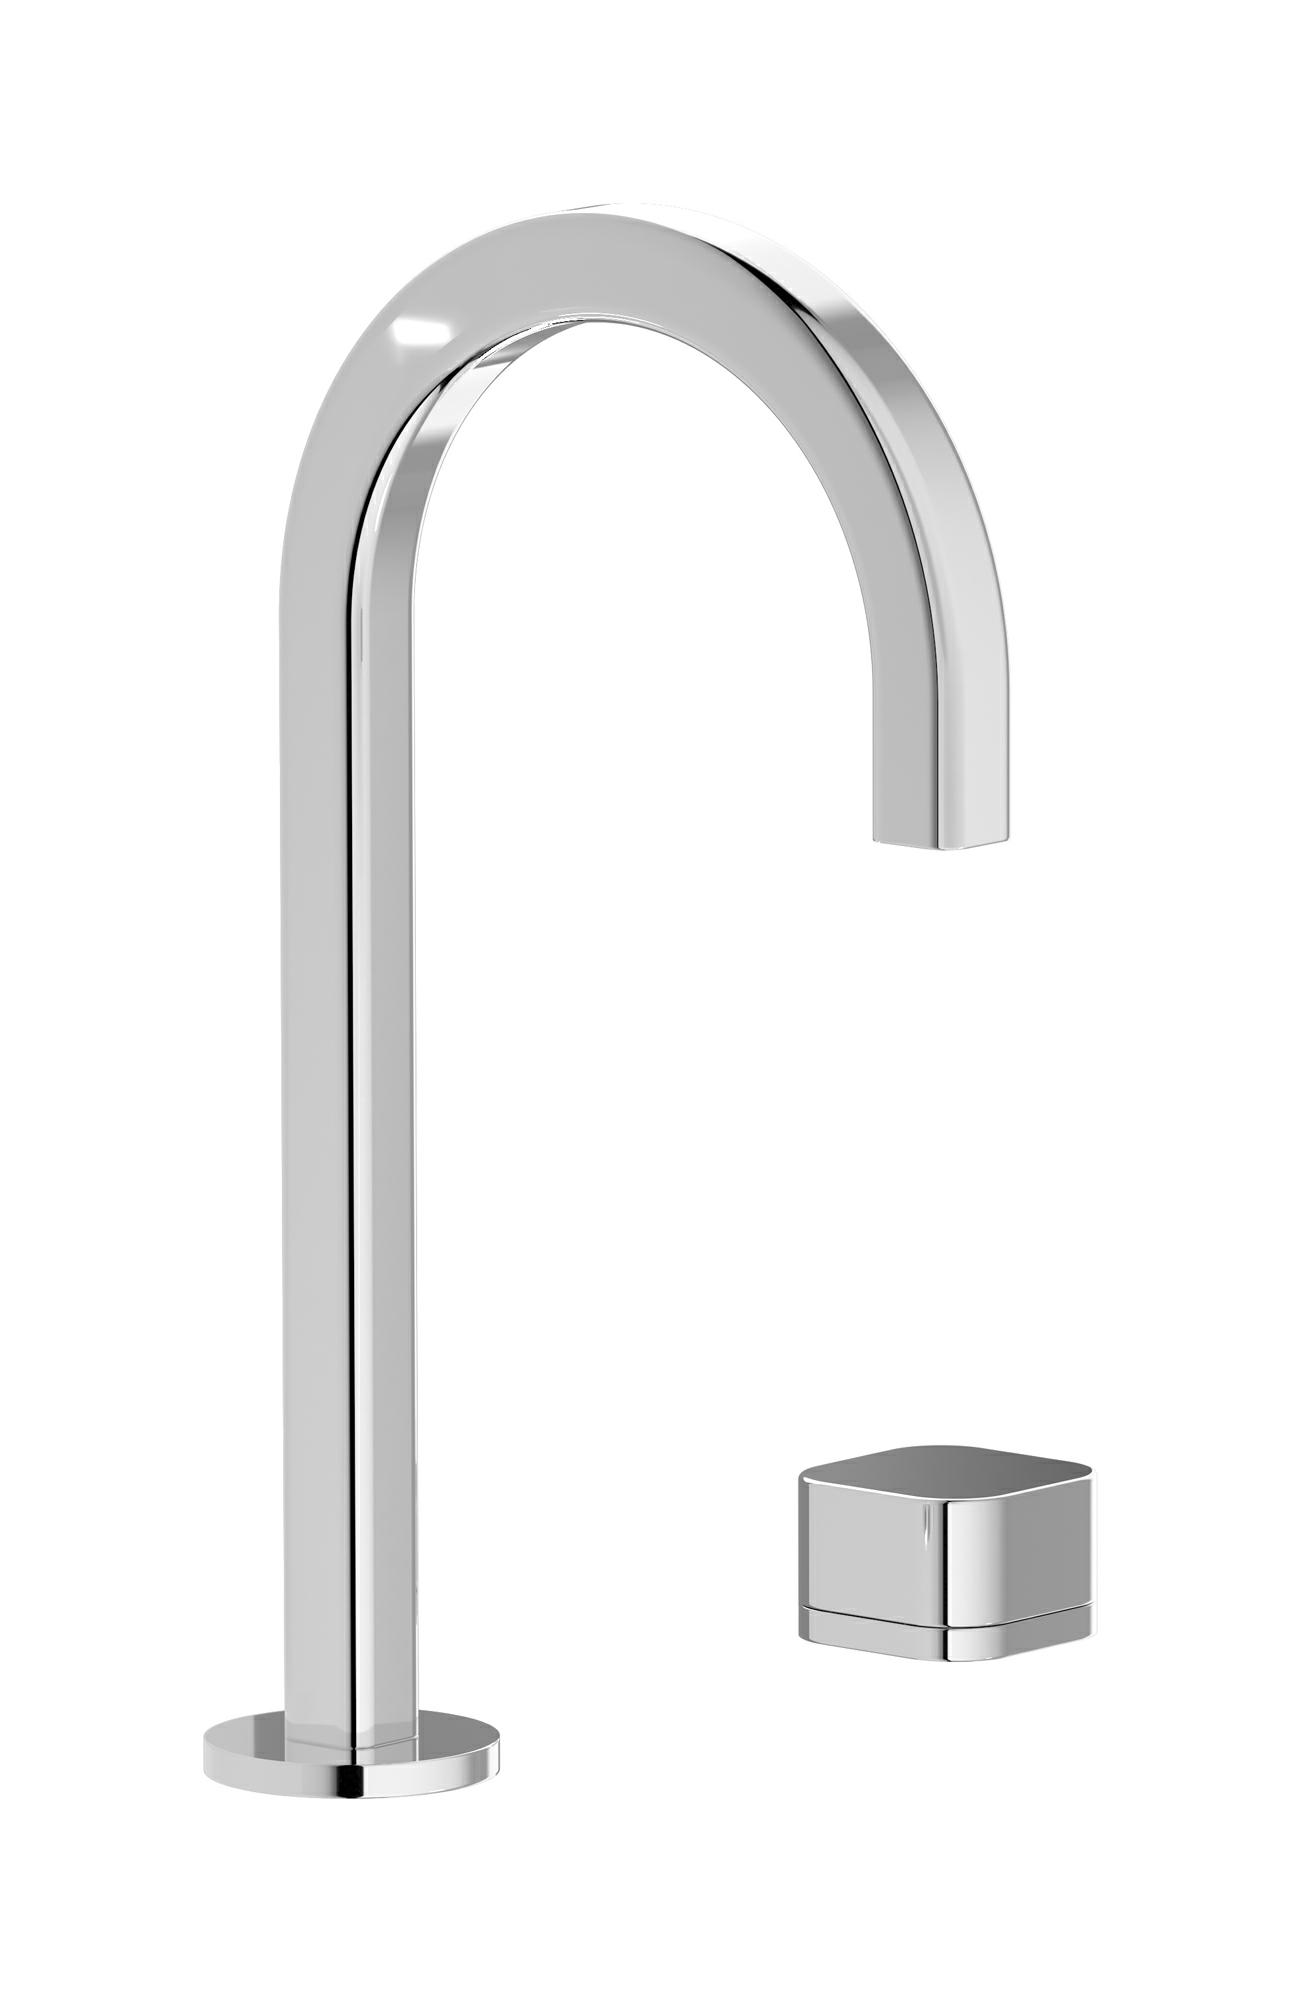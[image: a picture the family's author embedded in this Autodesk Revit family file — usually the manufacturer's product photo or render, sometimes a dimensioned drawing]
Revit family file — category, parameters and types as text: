
# Revit family: EO394_3
name_source: partatom
category: Apparecchi idraulici
units: mm (PartAtom-declared; Revit-internal decimal feet)

## family parameters
Basato su piano di lavoro = No
Condiviso = No
Mantieni orientamento annotazione = No
Numero OmniClass = 23.45.55.17
Punto di calcolo locali = No
Quota connettore circolare = Usa diametro
Sempre verticale = Sì
Taglio con vuoti quando caricato = No
Tipo di parte = Normale
Titolo OmniClass = Mixing Faucets

## types (12) — shared parameters
Cold water inlet = 10 mm  [stored 0.0328084 ft]
Commenti sul tipo = Washbasin
Connessione CW = No
Connessione HW = No
Connessione di scarico = No
Connessione di ventilazione = No
Descrizione = Washbasin two hole mixer
Hot water inlet = 10 mm  [stored 0.0328084 ft]
Produttore = IB Rubinetterie S.p.A.
URL = https://www.weareib.it
zero-valued in all types: Prospetto di default

## per-type parameters (varying)
| type | Finishes surface | Immagine tipo | Modello |
| Chrome | IB_Chrome | EO394CC_3.jpg | EO394CC_3 |
| Brushed nickel | IB_Brushed nickel | EO394SS_3.jpg | EO394SS_3 |
| Matt black | IB_matt black | EO394NP_3.jpg | EO394NP_3 |
| Natural brass | IB_Brass | EO394ON_3.jpg | EO394ON_3 |
| Black chrome | IB_Black chrome | EO394CF_3.jpg | EO394CF_3 |
| Brushed black chrome | IB_Brushed black chrome | EO394CS_3.jpg | EO394CS_3 |
| Pale gold | IB_Pale gold | EO394II_3.jpg | EO394II_3 |
| Brushed pale gold | IB_brushed pale gold | EO394IS_3.jpg | EO394IS_3 |
| Rose gold | IB_Rose gold | EO394RS_3.jpg | EO394RS_3 |
| Brushed rose gold | IB_Brushed rose gold | EO394SR_3.jpg | EO394SR_3 |
| Gold | IB_gold | EO394OO_3.jpg | EO394OO_3 |
| Brushed gold | IB_brushed gold | EO394OS_3.jpg | EO394OS_3 |

note: [stored X ft] marks values corroborated as IEEE doubles in the binary element streams (Revit-internal decimal feet)
